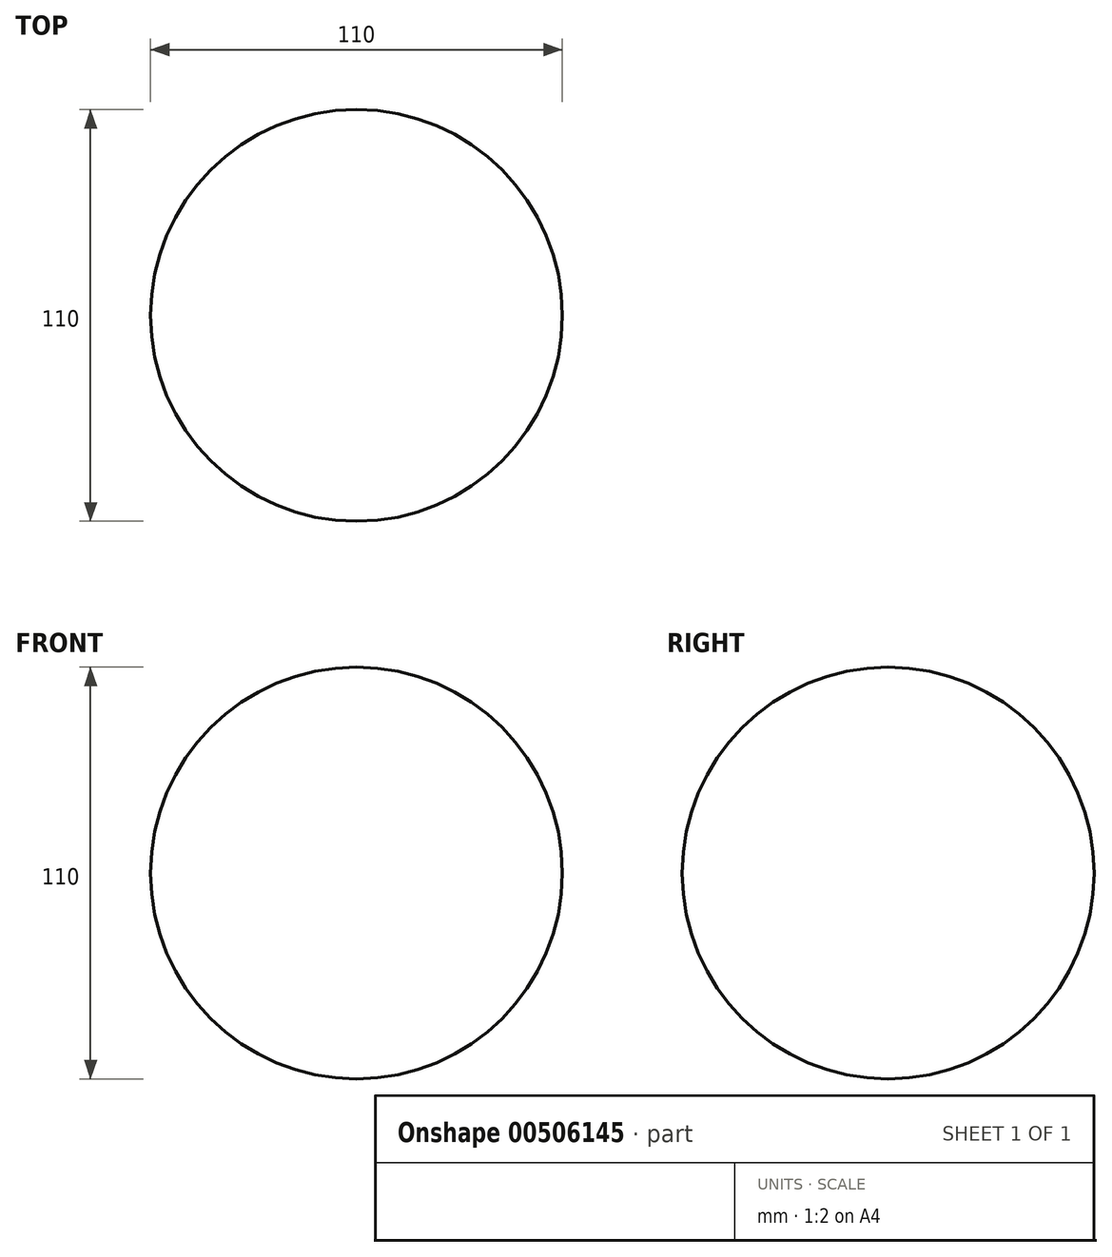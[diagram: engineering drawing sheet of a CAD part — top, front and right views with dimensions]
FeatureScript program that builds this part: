
annotation { "Feature Type Name" : "Feature", "Feature Type Description" : "" }
export const myFeature = defineFeature(function(context is Context, id is Id, definition is map)
    precondition{}
    {
        {
            var Q0;
            Q0=qCreatedBy(makeId("Front.planeOp"),FACE);
            var sketch = newSketch(context, id + "F0", { "sketchPlane" : qUnion([Q0])});
            skLineSegment(sketch, "E0", {"start": v(0, 55) * mm, "end": v(0, -55) * mm});
            skArc(sketch, "E1", {"start": v(0, -55) * mm, "mid": v(55, 0) * mm, "end": v(0, 55) * mm});
            skSolve(sketch);
        }
        {
            var Q0;
            Q0=qSketchRegion(id+"F0",true);
            var Q1;
            Q1=sQuery(id+"F0.wireOp",EDGE,"E0");
            revolve(context, id + "F1", {"entities" : qUnion([Q0]), "axis" : qUnion([Q1]), "revolveType" : RevolveType.FULL});
        }
    });
